# Revit family: S-758
name_source: partatom
category: Aparatos sanitarios
revit_build: Autodesk Revit 2015 (Build: 20140606_1530(x64)
units: mm (PartAtom-declared; Revit-internal decimal feet)

## types (6) — shared parameters
B = 52 mm
Comentarios de tipo = COMPATIBLE CON CERCOS VISTOS Y OCULTOS
Descripción = REJILLA PARA CANALETA, CLASSIC, PARA CANALETAS ANCHO 50
Fabricante = Jimten
Material = INOX AISI304
Modelo = S-758
Rejilla = INOX AISI304
URL = http://www.jimten.com

## per-type parameters (varying)
| type | A | Medida | N_MatrizHuecos | Referencia |
| 50x350mm_CLASSIC | 340 mm  [stored 1.11549 ft] | 350mm x 50mm | 5 | 13532 |
| 50x550mm_CLASSIC | 540 mm  [stored 1.77165 ft] | 550mm x 50mm | 9 | 13552 |
| 50x650mm_CLASSIC | 640 mm  [stored 2.09974 ft] | 650mm x 50mm | 11 | 13562 |
| 50x750mm_CLASSIC | 740 mm  [stored 2.42782 ft] | 750mm x 50mm | 13 | 13572 |
| 50x850mm_CLASSIC | 840 mm  [stored 2.75591 ft] | 850mm x 50mm | 14 | 13582 |
| 50x950mm_CLASSIC | 940 mm  [stored 3.08399 ft] | 950mm x 50mm | 16 | 13592 |

note: [stored X ft] marks values corroborated as IEEE doubles in the binary element streams (Revit-internal decimal feet)

## geometry (parser evidence)
native form markers: Blend x3, Sweep x2
no freeform markers — native parametric forms only
